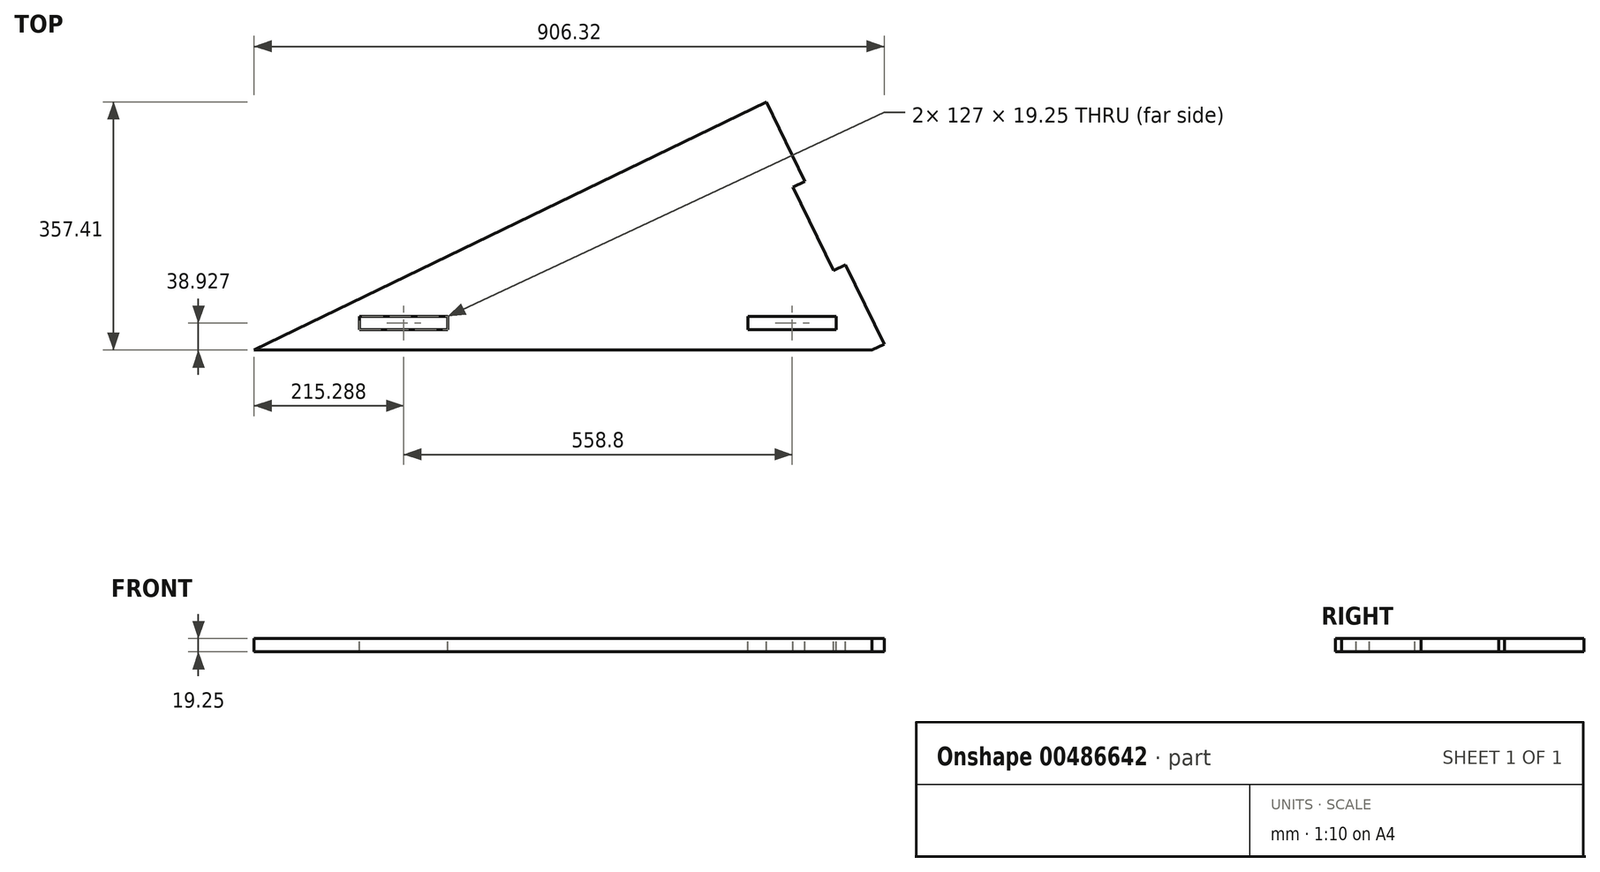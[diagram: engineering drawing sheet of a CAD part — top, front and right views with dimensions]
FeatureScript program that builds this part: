
annotation { "Feature Type Name" : "Feature", "Feature Type Description" : "" }
export const myFeature = defineFeature(function(context is Context, id is Id, definition is map)
    precondition{}
    {
        {
            var Q0;
            Q0=qCreatedBy(makeId("Top.planeOp"),FACE);
            var sketch = newSketch(context, id + "F0", { "sketchPlane" : qUnion([Q0])});
            skLineSegment(sketch, "E0", {"start": v(-698.62, 0) * mm, "end": v(190.38, 0) * mm});
            skLineSegment(sketch, "E1", {"start": v(190.38, 0) * mm, "end": v(21.14, 349.01) * mm});
            skLineSegment(sketch, "E2", {"start": v(21.14, 349.01) * mm, "end": v(-698.62, 0) * mm});
            skLineSegment(sketch, "E3", {"start": v(21.14, 349.01) * mm, "end": v(38.47, 357.41) * mm});
            skLineSegment(sketch, "E4", {"start": v(38.47, 357.41) * mm, "end": v(93.88, 243.14) * mm});
            skLineSegment(sketch, "E5", {"start": v(93.88, 243.14) * mm, "end": v(76.55, 234.74) * mm});
            skLineSegment(sketch, "E6", {"start": v(11.97, 29.3) * mm, "end": v(11.97, 48.55) * mm});
            skLineSegment(sketch, "E7", {"start": v(11.97, 48.55) * mm, "end": v(138.97, 48.55) * mm});
            skLineSegment(sketch, "E8", {"start": v(138.97, 48.55) * mm, "end": v(138.97, 29.3) * mm});
            skLineSegment(sketch, "E9", {"start": v(138.97, 29.3) * mm, "end": v(11.97, 29.3) * mm});
            skLineSegment(sketch, "E10", {"start": v(-419.83, 29.3) * mm, "end": v(-419.83, 48.55) * mm});
            skLineSegment(sketch, "E11", {"start": v(-419.83, 48.55) * mm, "end": v(-546.83, 48.55) * mm});
            skLineSegment(sketch, "E12", {"start": v(-546.83, 48.55) * mm, "end": v(-546.83, 29.3) * mm});
            skLineSegment(sketch, "E13", {"start": v(-546.83, 29.3) * mm, "end": v(-419.83, 29.3) * mm});
            skLineSegment(sketch, "E14", {"start": v(190.38, 0) * mm, "end": v(207.7, 8.4) * mm});
            skLineSegment(sketch, "E15", {"start": v(152.3, 122.67) * mm, "end": v(207.7, 8.4) * mm});
            skLineSegment(sketch, "E16", {"start": v(152.3, 122.67) * mm, "end": v(134.97, 114.27) * mm});
            skSolve(sketch);
        }
        {
            var Q0;
            {var subQ1=sQuery(id+"F0.wireOp",EDGE,"E0");Q0=makeQuery(id+"F0.imprint","IMPRINT",FACE,{"disambiguationData":[TD([[makeQuery(id+"F0.imprint","IMPRINT",EDGE,{"derivedFrom":subQ1}),1.0]])]});}
            var Q1;
            {var subQ0=sQuery(id+"F0.wireOp",EDGE,"E3");Q1=makeQuery(id+"F0.imprint","IMPRINT",FACE,{"disambiguationData":[TD([[makeQuery(id+"F0.imprint","IMPRINT",EDGE,{"derivedFrom":subQ0}),-1.0]])]});}
            var Q2;
            {var subQ0=sQuery(id+"F0.wireOp",EDGE,"E14");Q2=makeQuery(id+"F0.imprint","IMPRINT",FACE,{"disambiguationData":[TD([[makeQuery(id+"F0.imprint","IMPRINT",EDGE,{"derivedFrom":subQ0}),1.0]])]});}
            extrude(context, id + "F1", {"entities" : qUnion([Q0, Q1, Q2]), "oppositeDirection" : true, "depth" : 19.25 * mm, "offsetDistance" : 25.4 * mm});
        }
    });
